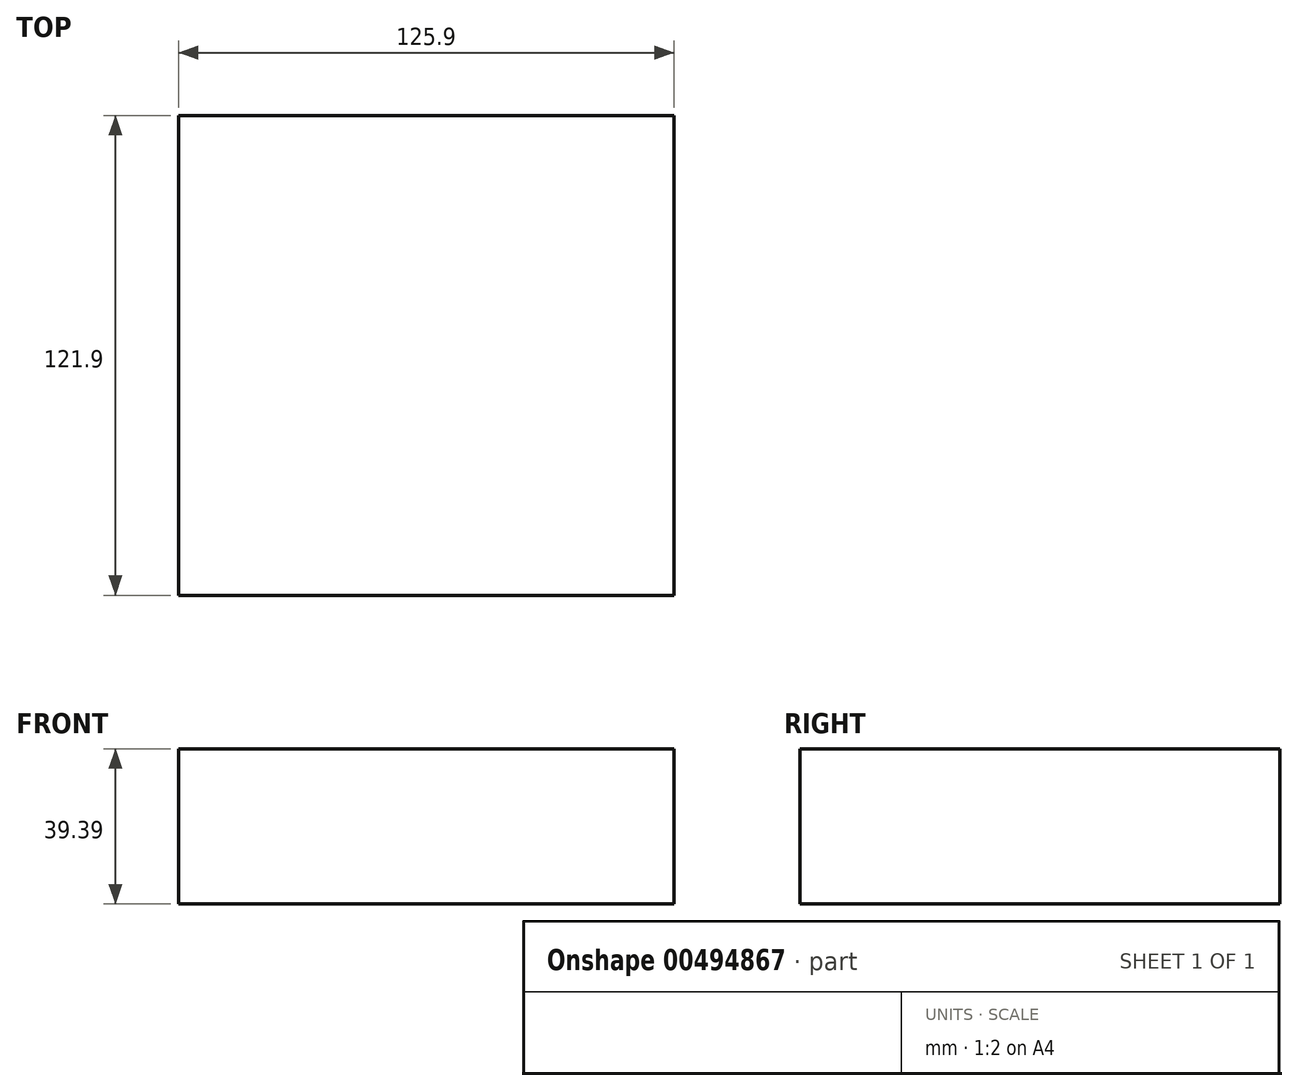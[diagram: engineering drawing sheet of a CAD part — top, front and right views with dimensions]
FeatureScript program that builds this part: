
annotation { "Feature Type Name" : "Feature", "Feature Type Description" : "" }
export const myFeature = defineFeature(function(context is Context, id is Id, definition is map)
    precondition{}
    {
        {
            var Q0;
            Q0=qCreatedBy(makeId("Right.planeOp"),FACE);
            var sketch = newSketch(context, id + "F0", { "sketchPlane" : qUnion([Q0])});
            skLineSegment(sketch, "E0.bottom", {"start": v(60.95, 21.6) * mm, "end": v(-60.95, 21.6) * mm});
            skLineSegment(sketch, "E0.top", {"start": v(60.95, 61) * mm, "end": v(-60.95, 61) * mm});
            skLineSegment(sketch, "E0.left", {"start": v(60.95, 21.6) * mm, "end": v(60.95, 61) * mm});
            skLineSegment(sketch, "E0.right", {"start": v(-60.95, 21.6) * mm, "end": v(-60.95, 61) * mm});
            skPoint(sketch, "E0.middle", {"position": v(0, 41.3) * mm});
            skSolve(sketch);
        }
        {
            var Q0;
            Q0=qSketchRegion(id+"F0",true);
            extrude(context, id + "F1", {"entities" : qUnion([Q0]), "depth" : 125.9 * mm});
        }
    });
